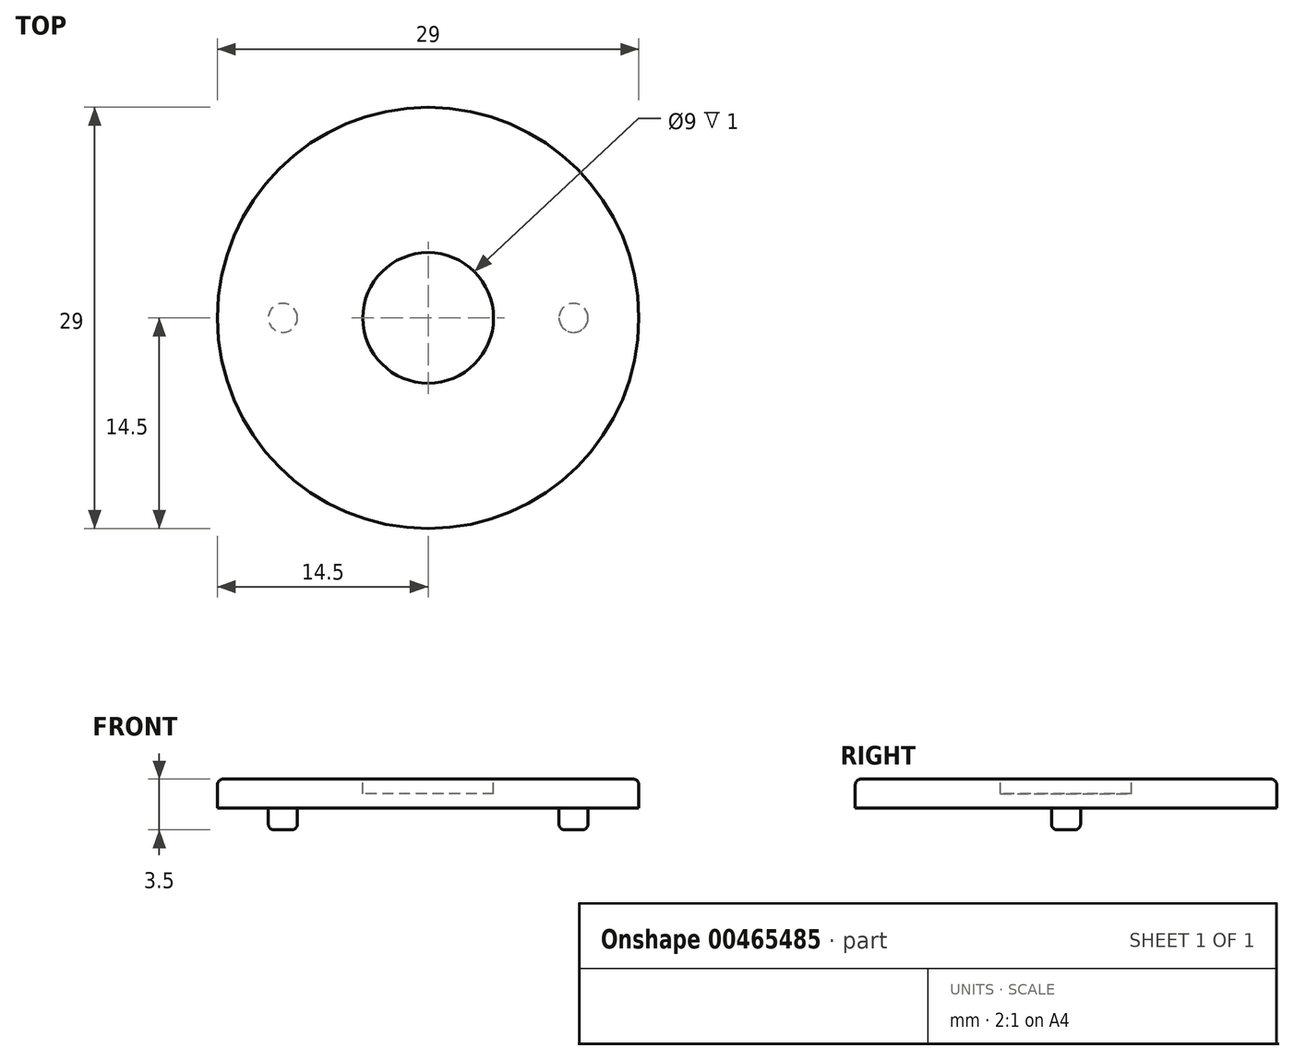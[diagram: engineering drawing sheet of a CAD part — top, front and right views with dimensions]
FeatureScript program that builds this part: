
annotation { "Feature Type Name" : "Feature", "Feature Type Description" : "" }
export const myFeature = defineFeature(function(context is Context, id is Id, definition is map)
    precondition{}
    {
        {
            var Q0;
            Q0=qCreatedBy(makeId("Top.planeOp"),FACE);
            var sketch = newSketch(context, id + "F0", { "sketchPlane" : qUnion([Q0])});
            skCircle(sketch, "E0", {"center": v(0, 0) * mm, "radius": 14.5 * mm});
            skSolve(sketch);
        }
        {
            var Q0;
            Q0 = qSketchRegion(id + "F0", true);
            extrude(context, id + "F1", {"entities" : qUnion([Q0]), "depth" : 2 * mm});
        }
        {
            var Q0;
            Q0=makeQuery(id+"F1.opExtrude","CAP_EDGE",EDGE,{"disambiguationData":[OSD([sQuery(id+"F0.wireOp",EDGE,"E0")])],"isStart":false});
            fillet(context, id + "F2", {"entities" : qUnion([Q0]), "radius" : 0.4 * mm, "tangentPropagation" : true, "allowEdgeOverflow" : false});
        }
        {
            var Q0;
            Q0=makeQuery(id+"F1.opExtrude","CAP_FACE",FACE,{"disambiguationData":[OSD([sQuery(id+"F0.wireOp",EDGE,"E0")])],"isStart":true});
            var sketch = newSketch(context, id + "F3", { "sketchPlane" : qUnion([Q0])});
            skCircle(sketch, "E1", {"center": v(-10, 0) * mm, "radius": 1 * mm});
            skCircle(sketch, "E2", {"center": v(10, 0) * mm, "radius": 1 * mm});
            skSolve(sketch);
        }
        {
            var Q0;
            Q0 = qSketchRegion(id + "F3", true);
            extrude(context, id + "F4", {"entities" : qUnion([Q0]), "operationType" : NewBodyOperationType.ADD, "depth" : 1.5 * mm});
        }
        {
            var Q0;
            Q0=makeQuery(id+"F4.opExtrude","CAP_EDGE",EDGE,{"disambiguationData":[OSD([sQuery(id+"F3.wireOp",EDGE,"E1")])],"isStart":false});
            var Q1;
            Q1=makeQuery(id+"F4.opExtrude","CAP_EDGE",EDGE,{"disambiguationData":[OSD([sQuery(id+"F3.wireOp",EDGE,"E2")])],"isStart":false});
            fillet(context, id + "F5", {"entities" : qUnion([Q0, Q1]), "radius" : 0.4 * mm, "tangentPropagation" : true, "allowEdgeOverflow" : false});
        }
        {
            var Q0;
            Q0=makeQuery(id+"F1.opExtrude","CAP_FACE",FACE,{"disambiguationData":[OSD([sQuery(id+"F0.wireOp",EDGE,"E0")])],"isStart":false});
            var sketch = newSketch(context, id + "F6", { "sketchPlane" : qUnion([Q0])});
            skCircle(sketch, "E3", {"center": v(0, 0) * mm, "radius": 4.5 * mm});
            skSolve(sketch);
        }
        {
            var Q0;
            Q0 = qSketchRegion(id + "F6", true);
            extrude(context, id + "F7", {"entities" : qUnion([Q0]), "operationType" : NewBodyOperationType.REMOVE, "oppositeDirection" : true, "depth" : 1 * mm});
        }
    });
